# Revit family: Deca_Válvula de Escoamento_1601.C
name_source: partatom
category: Plumbing Fixtures
revit_build: Autodesk Revit Architecture 2012 (Build: 20110916_2132(x64)
units: mm (PartAtom-declared; Revit-internal decimal feet)

## types (3) — shared parameters
Aprovado por = Contino/quattroD
Assembly Code = D2020
Atendimento ao Cliente = 0800-0117073
Consumo = Varia com a pressão
Criado por = Contino/quattroD
Description = Válvula de escoamento Luxo para lavatório / cuba / bidê
Diâmetro Água Fria = 15 mm  [stored 0.0492126 ft]
Flow Pressure = 0.00 psi
Informações Complementares = Não Aplicável
Linha = Válvula de Escoamento
Louça/Metais = Metal
Manufacturer = Deca
Material = Latão Cromado e Plástico de Engenharia
Norma = ABNT NBR 15423:2006
Peso Liquido (Kg) = 0.175
Pressão = 2 A 40 mca
Produto = Válvula de escoamento Luxo para lavatório / cuba / bidê
Raio Água Fria = 8 mm  [stored 0.0262467 ft]
Segmento = Luxo
URL = www.deca.com.br/produtos
Variações de COR = Cromado (1601.C), Preto Fosco (1602.F.PTO); Gold (1601.D.GLD)
Vendido Separadamente = Não Aplicável
zero-valued in all types: CWFU, Default Elevation, WFU

## per-type parameters (varying)
| type | Código | Model | Válvula |
| 1601.C_Cromado CR10 | 1601.C | 1601.C | Deca CR10 Cromado Metal |
| 1602.F.PTO_Preto Fosco | 1602.F.PTO | 1602.F.PTO | Deca PR15 Preto Fosco Metal |
| 1601.D.GLD_Gold | 1601.D.GLD | 1601.D.GLD | Deca GLD Gold Metal |

note: [stored X ft] marks values corroborated as IEEE doubles in the binary element streams (Revit-internal decimal feet)

## geometry (parser evidence)
native form markers: Blend x2, Sweep x1
no freeform markers — native parametric forms only
